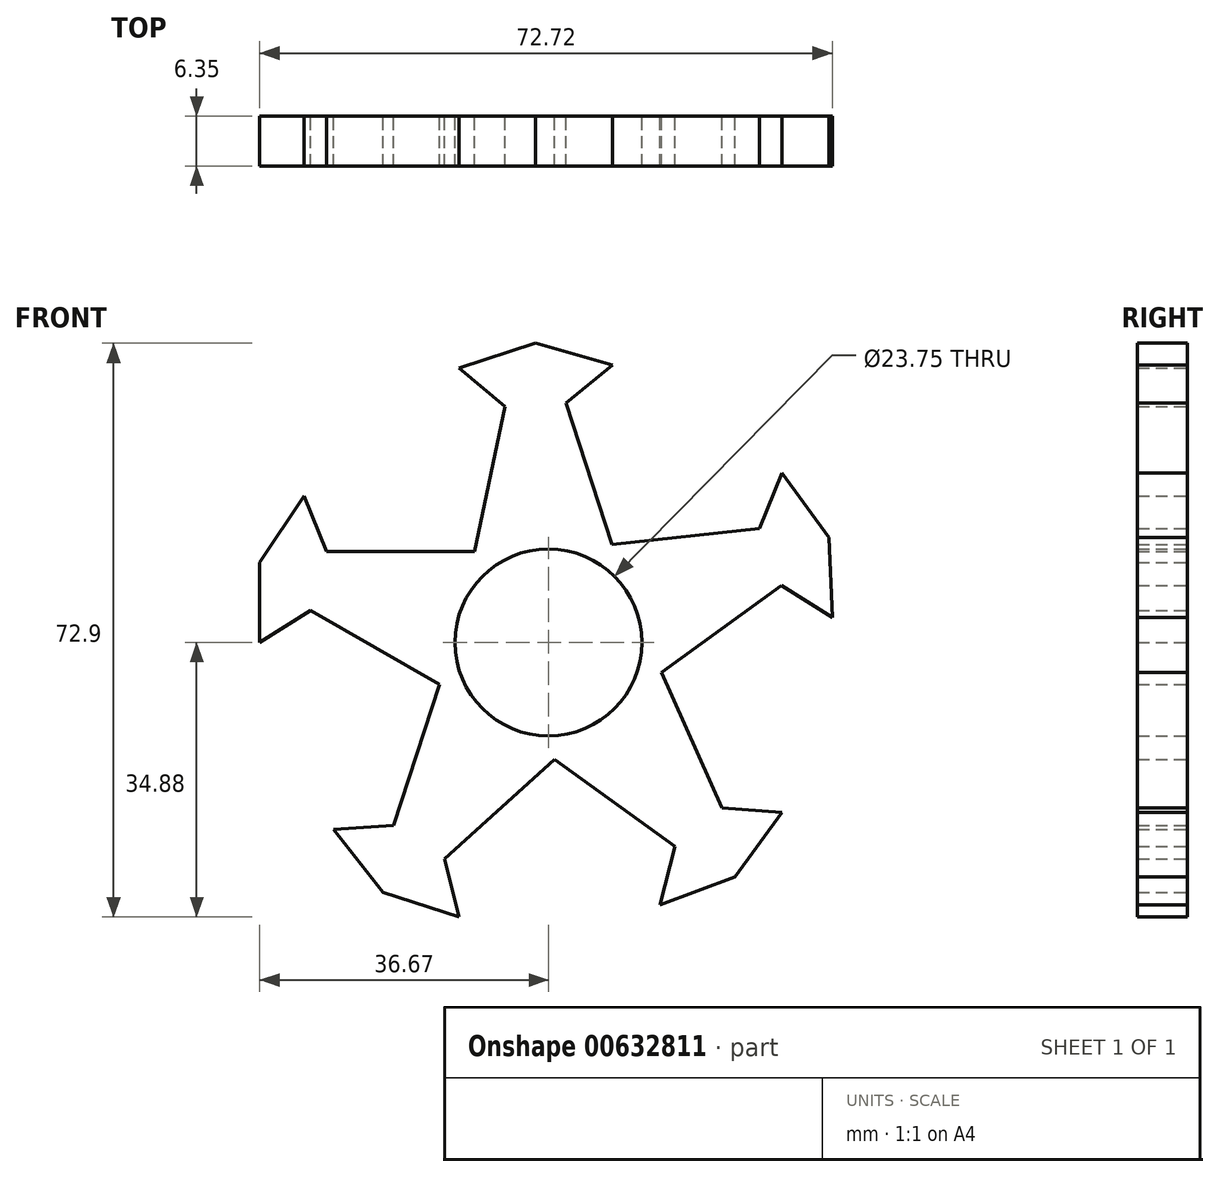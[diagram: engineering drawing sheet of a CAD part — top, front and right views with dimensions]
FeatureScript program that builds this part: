
annotation { "Feature Type Name" : "Feature", "Feature Type Description" : "" }
export const myFeature = defineFeature(function(context is Context, id is Id, definition is map)
    precondition{}
    {
        {
            var Q0;
            Q0=qCreatedBy(makeId("Front.planeOp"),FACE);
            var sketch = newSketch(context, id + "F0", { "sketchPlane" : qUnion([Q0])});
            skCircle(sketch, "E0", {"center": v(0, 0) * mm, "radius": 11.87 * mm});
            skLineSegment(sketch, "E1", {"start": v(-9.37, 11.54) * mm, "end": v(-28.21, 11.54) * mm});
            skLineSegment(sketch, "E2", {"start": v(-13.87, -5.34) * mm, "end": v(-30.21, 4.04) * mm});
            skLineSegment(sketch, "E3", {"start": v(-28.21, 11.54) * mm, "end": v(-31.04, 18.61) * mm});
            skLineSegment(sketch, "E4", {"start": v(-31.04, 18.61) * mm, "end": v(-36.67, 10.16) * mm});
            skLineSegment(sketch, "E5", {"start": v(-36.67, 10.16) * mm, "end": v(-36.67, 0) * mm});
            skLineSegment(sketch, "E6", {"start": v(-36.67, 0) * mm, "end": v(-30.21, 4.04) * mm});
            skLineSegment(sketch, "E7.1.0", {"start": v(0.8, -14.84) * mm, "end": v(-13.18, -27.48) * mm});
            skLineSegment(sketch, "E7.2.0", {"start": v(14.36, -3.83) * mm, "end": v(22.07, -21.03) * mm});
            skLineSegment(sketch, "E8.1.0", {"start": v(-27.3, -23.77) * mm, "end": v(-21, -31.74) * mm});
            skLineSegment(sketch, "E8.1.1", {"start": v(-11.33, -34.88) * mm, "end": v(-13.18, -27.48) * mm});
            skLineSegment(sketch, "E8.1.2", {"start": v(-13.87, -5.34) * mm, "end": v(-19.7, -23.27) * mm});
            skLineSegment(sketch, "E8.1.3", {"start": v(-19.7, -23.27) * mm, "end": v(-27.3, -23.77) * mm});
            skLineSegment(sketch, "E8.1.4", {"start": v(-21, -31.74) * mm, "end": v(-11.33, -34.88) * mm});
            skLineSegment(sketch, "E8.2.0", {"start": v(14.17, -33.3) * mm, "end": v(23.7, -29.78) * mm});
            skLineSegment(sketch, "E8.2.1", {"start": v(29.67, -21.56) * mm, "end": v(22.07, -21.03) * mm});
            skLineSegment(sketch, "E8.2.2", {"start": v(0.8, -14.84) * mm, "end": v(16.04, -25.92) * mm});
            skLineSegment(sketch, "E8.2.3", {"start": v(16.04, -25.92) * mm, "end": v(14.17, -33.3) * mm});
            skLineSegment(sketch, "E8.2.4", {"start": v(23.7, -29.78) * mm, "end": v(29.67, -21.56) * mm});
            skLineSegment(sketch, "E9.2.3.0", {"start": v(8.08, 12.47) * mm, "end": v(26.82, 14.5) * mm});
            skLineSegment(sketch, "E9.2.4.0", {"start": v(-9.37, 11.54) * mm, "end": v(-5.5, 29.98) * mm});
            skLineSegment(sketch, "E10.3.3.0", {"start": v(29.67, 21.56) * mm, "end": v(26.82, 14.5) * mm});
            skLineSegment(sketch, "E10.6.3.0", {"start": v(14.36, -3.83) * mm, "end": v(29.6, 7.25) * mm});
            skLineSegment(sketch, "E10.8.3.0", {"start": v(36.05, 3.18) * mm, "end": v(35.64, 13.34) * mm});
            skLineSegment(sketch, "E10.9.3.0", {"start": v(29.6, 7.25) * mm, "end": v(36.05, 3.18) * mm});
            skLineSegment(sketch, "E10.12.3.0", {"start": v(35.64, 13.34) * mm, "end": v(29.67, 21.56) * mm});
            skLineSegment(sketch, "E10.3.4.0", {"start": v(-11.33, 34.88) * mm, "end": v(-5.5, 29.98) * mm});
            skLineSegment(sketch, "E10.6.4.0", {"start": v(8.08, 12.47) * mm, "end": v(2.25, 30.4) * mm});
            skLineSegment(sketch, "E10.8.4.0", {"start": v(8.11, 35.27) * mm, "end": v(-1.67, 38.02) * mm});
            skLineSegment(sketch, "E10.9.4.0", {"start": v(2.25, 30.4) * mm, "end": v(8.11, 35.27) * mm});
            skLineSegment(sketch, "E10.12.4.0", {"start": v(-1.67, 38.02) * mm, "end": v(-11.33, 34.88) * mm});
            skPoint(sketch, "E11.orphan", {"position": v(-10.71, 5.12) * mm});
            skPoint(sketch, "E12.orphan", {"position": v(-2.81, 11.54) * mm});
            skPoint(sketch, "E13.orphan", {"position": v(-11.84, 0.9) * mm});
            skPoint(sketch, "E14.orphan", {"position": v(-8.18, -8.6) * mm});
            skPoint(sketch, "E15.orphan", {"position": v(-4.5, -10.99) * mm});
            skPoint(sketch, "E16.orphan", {"position": v(5.66, -10.44) * mm});
            skPoint(sketch, "E17.orphan", {"position": v(9.06, -7.68) * mm});
            skPoint(sketch, "E18.orphan", {"position": v(11.68, 2.15) * mm});
            skPoint(sketch, "E19.orphan", {"position": v(10.1, 6.24) * mm});
            skPoint(sketch, "E20.orphan", {"position": v(1.56, 11.77) * mm});
            skSolve(sketch);
        }
        {
            var Q0;
            {var subQ1=sQuery(id+"F0.wireOp",EDGE,"E1");Q0=makeQuery(id+"F0.imprint","IMPRINT",FACE,{"disambiguationData":[TD([[makeQuery(id+"F0.imprint","IMPRINT",EDGE,{"derivedFrom":subQ1}),1.0]])]});}
            extrude(context, id + "F1", {"entities" : qUnion([Q0]), "depth" : 6.35 * mm, "offsetDistance" : 25.4 * mm});
        }
    });
